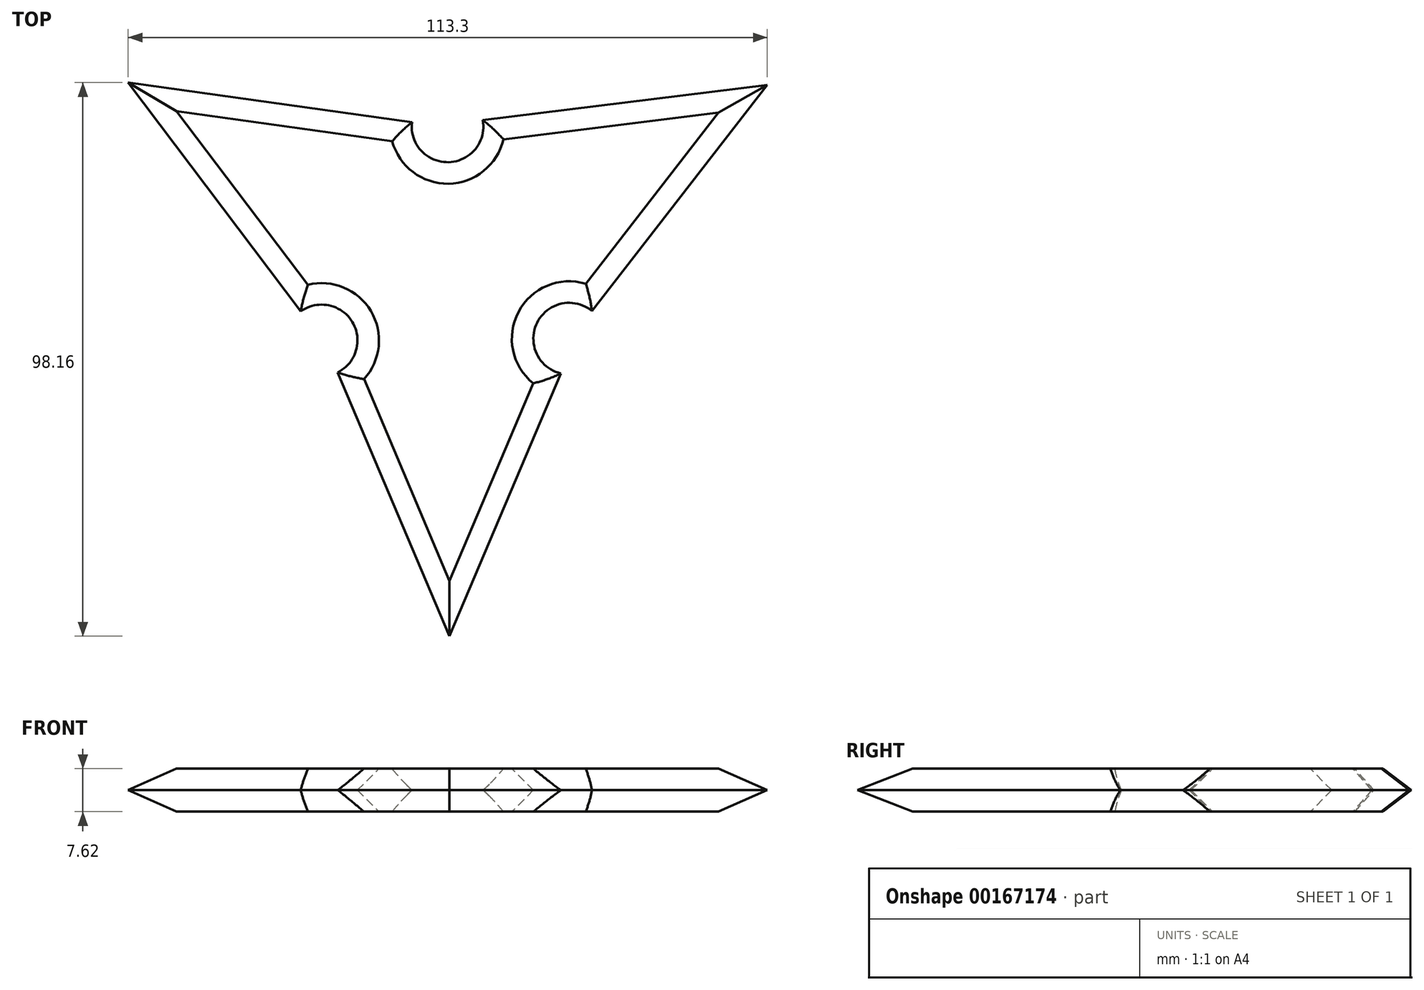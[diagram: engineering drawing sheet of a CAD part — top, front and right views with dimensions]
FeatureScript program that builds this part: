
annotation { "Feature Type Name" : "Feature", "Feature Type Description" : "" }
export const myFeature = defineFeature(function(context is Context, id is Id, definition is map)
    precondition{}
    {
        {
            var Q0;
            Q0=qCreatedBy(makeId("Top.planeOp"),FACE);
            var sketch = newSketch(context, id + "F0", { "sketchPlane" : qUnion([Q0])});
            skLineSegment(sketch, "E0", {"start": v(-0.48, -51.27) * mm, "end": v(19.24, -4.68) * mm});
            skLineSegment(sketch, "E1.1.0", {"start": v(-57.45, 46.89) * mm, "end": v(-26.83, 6.35) * mm});
            skLineSegment(sketch, "E1.1.1", {"start": v(-7.13, 39.87) * mm, "end": v(-57.45, 46.89) * mm});
            skLineSegment(sketch, "E1.2.0", {"start": v(55.85, 46.46) * mm, "end": v(5.43, 40.22) * mm});
            skLineSegment(sketch, "E1.2.1", {"start": v(24.76, 6.4) * mm, "end": v(55.85, 46.46) * mm});
            skLineSegment(sketch, "E2.MirrorCS", {"start": v(-0.48, -51.27) * mm, "end": v(-20.29, -4.5) * mm});
            skArc(sketch, "E3", {"start": v(24.76, 6.4) * mm, "mid": v(15.04, 4.33) * mm, "end": v(19.24, -4.68) * mm});
            skArc(sketch, "E4", {"start": v(-7.13, 39.87) * mm, "mid": v(-0.65, 32.79) * mm, "end": v(5.43, 40.22) * mm});
            skArc(sketch, "E5", {"start": v(-20.29, -4.5) * mm, "mid": v(-17.7, 4.46) * mm, "end": v(-26.83, 6.35) * mm});
            skSolve(sketch);
        }
        {
            var Q0;
            Q0 = qSketchRegion(id + "F0", true);
            var Q1;
            Q1=makeQuery(id+"F0.imprint","IMPRINT",FACE,{"disambiguationData":[TD([[makeQuery(id+"F0.imprint","IMPRINT",EDGE,{"derivedFrom":sQuery(id+"F0.wireOp",EDGE,"f6664266-9b28-43ca-81fb-3f2bc8e758a5.0")}),1.0]])]});
            extrude(context, id + "F1", {"entities" : qUnion([Q0, Q1]), "depth" : 7.62 * mm});
        }
        {
            var Q0;
            Q0=makeQuery(id+"F1.opExtrude","CAP_EDGE",EDGE,{"disambiguationData":[OSD([sQuery(id+"F0.wireOp",EDGE,"E1.1.1")])],"isStart":true});
            var Q1;
            Q1=makeQuery(id+"F1.opExtrude","CAP_EDGE",EDGE,{"disambiguationData":[OSD([sQuery(id+"F0.wireOp",EDGE,"E1.2.0")])],"isStart":true});
            var Q2;
            Q2=makeQuery(id+"F1.opExtrude","CAP_EDGE",EDGE,{"disambiguationData":[OSD([sQuery(id+"F0.wireOp",EDGE,"E1.1.0")])],"isStart":true});
            var Q3;
            Q3=makeQuery(id+"F1.opExtrude","CAP_EDGE",EDGE,{"disambiguationData":[OSD([sQuery(id+"F0.wireOp",EDGE,"E1.2.1")])],"isStart":true});
            var Q4;
            Q4=makeQuery(id+"F1.opExtrude","CAP_EDGE",EDGE,{"disambiguationData":[OSD([sQuery(id+"F0.wireOp",EDGE,"E0")])],"isStart":true});
            var Q5;
            Q5=makeQuery(id+"F1.opExtrude","CAP_EDGE",EDGE,{"disambiguationData":[OSD([sQuery(id+"F0.wireOp",EDGE,"E2.MirrorCS")])],"isStart":true});
            var Q6;
            Q6=makeQuery(id+"F1.opExtrude","CAP_EDGE",EDGE,{"disambiguationData":[OSD([sQuery(id+"F0.wireOp",EDGE,"09dcea2b-e624-4583-a6d0-5984cace15520.MirrorCS")])],"isStart":true});
            var Q7;
            Q7=makeQuery(id+"F1.opExtrude","CAP_EDGE",EDGE,{"disambiguationData":[OSD([sQuery(id+"F0.wireOp",EDGE,"E3")])],"isStart":true});
            var Q8;
            Q8=makeQuery(id+"F1.opExtrude","CAP_EDGE",EDGE,{"disambiguationData":[OSD([sQuery(id+"F0.wireOp",EDGE,"5m71L1i9-UdIz-sZnb-xXu5-8nS6wcuZGs47")])],"isStart":true});
            chamfer(context, id + "F2", {"entities" : qUnion([Q0, Q1, Q2, Q3, Q4, Q5, Q6, Q7, Q8]), "width" : 3.8 * mm, "tangentPropagation" : true});
        }
        {
            var Q0;
            Q0=makeQuery(id+"F1.opExtrude","CAP_EDGE",EDGE,{"disambiguationData":[OSD([sQuery(id+"F0.wireOp",EDGE,"E1.1.1")])],"isStart":false});
            var Q1;
            Q1=makeQuery(id+"F1.opExtrude","CAP_EDGE",EDGE,{"disambiguationData":[OSD([sQuery(id+"F0.wireOp",EDGE,"E1.1.0")])],"isStart":false});
            var Q2;
            Q2=makeQuery(id+"F1.opExtrude","CAP_EDGE",EDGE,{"disambiguationData":[OSD([sQuery(id+"F0.wireOp",EDGE,"E2.MirrorCS")])],"isStart":false});
            var Q3;
            Q3=makeQuery(id+"F1.opExtrude","CAP_EDGE",EDGE,{"disambiguationData":[OSD([sQuery(id+"F0.wireOp",EDGE,"E0")])],"isStart":false});
            var Q4;
            Q4=makeQuery(id+"F1.opExtrude","CAP_EDGE",EDGE,{"disambiguationData":[OSD([sQuery(id+"F0.wireOp",EDGE,"E1.2.1")])],"isStart":false});
            var Q5;
            Q5=makeQuery(id+"F1.opExtrude","CAP_EDGE",EDGE,{"disambiguationData":[OSD([sQuery(id+"F0.wireOp",EDGE,"E1.2.0")])],"isStart":false});
            var Q6;
            Q6=makeQuery(id+"F1.opExtrude","CAP_EDGE",EDGE,{"disambiguationData":[OSD([sQuery(id+"F0.wireOp",EDGE,"5m71L1i9-UdIz-sZnb-xXu5-8nS6wcuZGs47")])],"isStart":false});
            var Q7;
            Q7=makeQuery(id+"F1.opExtrude","CAP_EDGE",EDGE,{"disambiguationData":[OSD([sQuery(id+"F0.wireOp",EDGE,"E3")])],"isStart":false});
            var Q8;
            Q8=makeQuery(id+"F1.opExtrude","CAP_EDGE",EDGE,{"disambiguationData":[OSD([sQuery(id+"F0.wireOp",EDGE,"09dcea2b-e624-4583-a6d0-5984cace15520.MirrorCS")])],"isStart":false});
            var Q9;
            Q9=makeQuery(id+"F1.opExtrude","CAP_EDGE",EDGE,{"disambiguationData":[OSD([sQuery(id+"F0.wireOp",EDGE,"E4")])],"isStart":false});
            var Q10;
            Q10=makeQuery(id+"F1.opExtrude","CAP_EDGE",EDGE,{"disambiguationData":[OSD([sQuery(id+"F0.wireOp",EDGE,"E5")])],"isStart":false});
            var Q11;
            Q11=makeQuery(id+"F1.opExtrude","CAP_EDGE",EDGE,{"disambiguationData":[OSD([sQuery(id+"F0.wireOp",EDGE,"E5")])],"isStart":true});
            var Q12;
            Q12=makeQuery(id+"F1.opExtrude","CAP_EDGE",EDGE,{"disambiguationData":[OSD([sQuery(id+"F0.wireOp",EDGE,"E4")])],"isStart":true});
            chamfer(context, id + "F3", {"entities" : qUnion([Q0, Q1, Q2, Q3, Q4, Q5, Q6, Q7, Q8, Q9, Q10, Q11, Q12]), "width" : 3.8 * mm, "tangentPropagation" : true});
        }
    });
